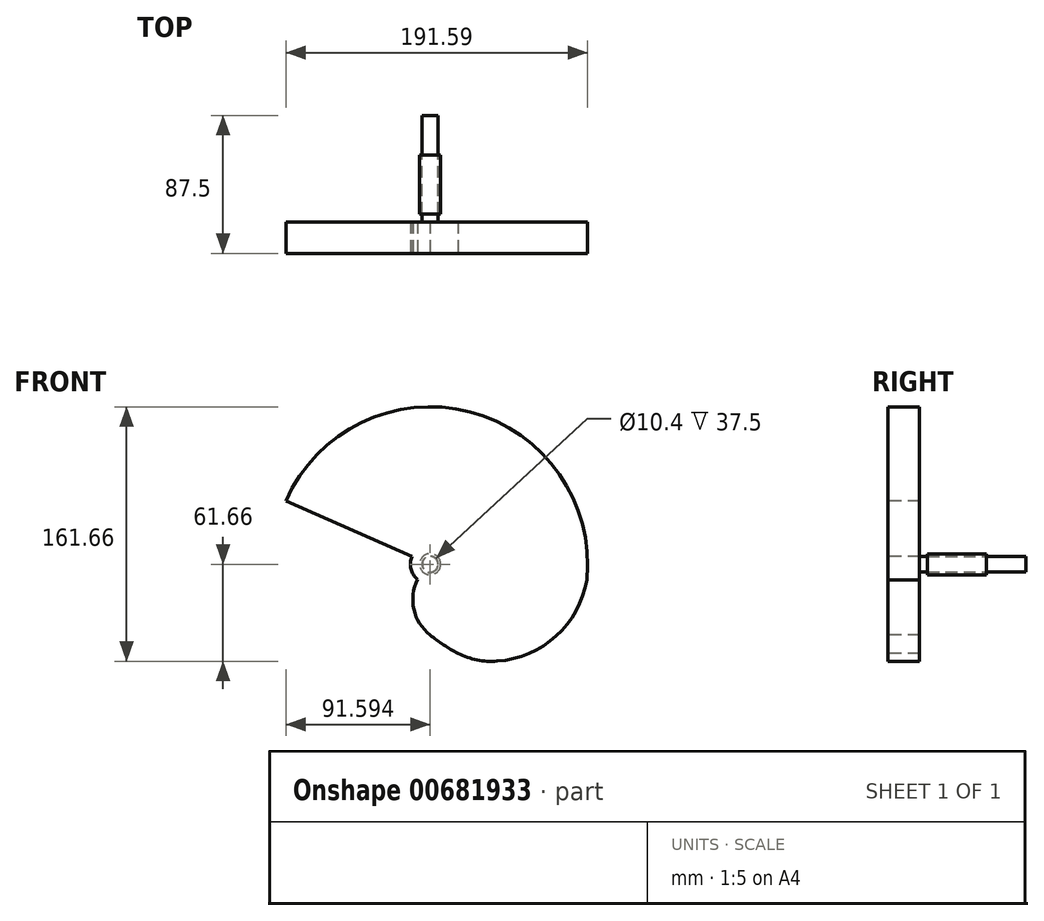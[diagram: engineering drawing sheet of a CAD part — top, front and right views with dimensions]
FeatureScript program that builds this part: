
annotation { "Feature Type Name" : "Feature", "Feature Type Description" : "" }
export const myFeature = defineFeature(function(context is Context, id is Id, definition is map)
    precondition{}
    {
        {
            var Q0;
            Q0=qCreatedBy(makeId("Front.planeOp"),FACE);
            var sketch = newSketch(context, id + "F0", { "sketchPlane" : qUnion([Q0])});
            skCircle(sketch, "E0", {"center": v(-51.72, 0) * mm, "radius": 5 * mm});
            skCircle(sketch, "E1", {"center": v(-51.72, 0) * mm, "radius": 5.2 * mm});
            skCircle(sketch, "E2", {"center": v(-51.72, 0) * mm, "radius": 6.7 * mm});
            skSolve(sketch);
        }
        {
            var Q0;
            Q0=makeQuery(id+"F0.imprint","IMPRINT",FACE,{"disambiguationData":[TD([[makeQuery(id+"F0.imprint","IMPRINT",EDGE,{"derivedFrom":sQuery(id+"F0.wireOp",EDGE,"E0")}),1.0]])]});
            var Q1;
            Q1=makeQuery(id+"F0.imprint","IMPRINT",FACE,{"disambiguationData":[TD([[makeQuery(id+"F0.imprint","IMPRINT",EDGE,{"derivedFrom":sQuery(id+"F0.wireOp",EDGE,"E1")}),-1.0]])]});
            extrude(context, id + "F1", {"entities" : qUnion([Q0, Q1]), "endBound" : BoundingType.SYMMETRIC, "depth" : 37.5 * mm, "offsetDistance" : 25 * mm});
        }
        {
            var Q0;
            Q0=makeQuery(id+"F1.opExtrude","CAP_FACE",FACE,{"disambiguationData":[OSD([sQuery(id+"F0.wireOp",EDGE,"E0")])],"isStart":false});
            extrude(context, id + "F2", {"entities" : qUnion([Q0]), "operationType" : NewBodyOperationType.ADD, "depth" : 25 * mm, "offsetDistance" : 25 * mm});
        }
        {
            var Q0;
            Q0=makeQuery(id+"F1.opExtrude","CAP_FACE",FACE,{"disambiguationData":[OSD([sQuery(id+"F0.wireOp",EDGE,"E0")])],"isStart":true});
            extrude(context, id + "F3", {"entities" : qUnion([Q0]), "operationType" : NewBodyOperationType.ADD, "depth" : 25 * mm, "offsetDistance" : 25 * mm});
        }
        {
            var Q0;
            Q0=makeQuery(id+"F2.opExtrude","CAP_FACE",FACE,{"disambiguationData":[OSD([sQuery(id+"F0.wireOp",EDGE,"E0")])],"isStart":false});
            var sketch = newSketch(context, id + "F4", { "sketchPlane" : qUnion([Q0])});
            skCircle(sketch, "E3", {"center": v(-51.72, 0) * mm, "radius": 100 * mm});
            skSolve(sketch);
        }
        {
            var Q0;
            Q0=makeQuery(id+"F4.imprint","IMPRINT",FACE,{"disambiguationData":[TD([[makeQuery(id+"F4.imprint","IMPRINT",EDGE,{"derivedFrom":sQuery(id+"F4.wireOp",EDGE,"E3")}),1.0]])]});
            extrude(context, id + "F5", {"entities" : qUnion([Q0]), "operationType" : NewBodyOperationType.ADD, "oppositeDirection" : true, "depth" : 20 * mm, "offsetDistance" : 25 * mm});
        }
        {
            var Q0;
            {var subQ0=sQuery(id+"F0.wireOp",EDGE,"E0");Q0=makeQuery(id+"F5.boolean.opBoolean","MERGE",FACE,{"derivedFrom":[makeQuery(id+"F2.opExtrude","CAP_FACE",FACE,{"disambiguationData":[OSD([subQ0])],"isStart":false}),makeQuery(id+"F5.opExtrude","CAP_FACE",FACE,{"disambiguationData":[OSD([subQ0,sQuery(id+"F4.wireOp",EDGE,"E3")])],"isStart":true})]});}
            var sketch = newSketch(context, id + "F6", { "sketchPlane" : qUnion([Q0])});
            skLineSegment(sketch, "E4", {"start": v(-51.72, 0) * mm, "end": v(-143.3, 40.14) * mm});
            skArc(sketch, "E5", {"start": v(-51.72, 0) * mm, "mid": v(-62.72, -22.48) * mm, "end": v(-51.72, -44.96) * mm});
            skArc(sketch, "E6", {"start": v(-51.72, -44.96) * mm, "mid": v(-17.5, -63.5) * mm, "end": v(21.08, -68.56) * mm});
            skArc(sketch, "E7", {"start": v(-9.11, -61.54) * mm, "mid": v(28.3, -45.57) * mm, "end": v(47.8, -9.86) * mm});
            skArc(sketch, "E8", {"start": v(-33.95, -56.6) * mm, "mid": v(-21.86, -60.75) * mm, "end": v(-9.11, -61.54) * mm});
            skCircle(sketch, "E9", {"center": v(-51.72, 0) * mm, "radius": 12.5 * mm});
            skSolve(sketch);
        }
        {
            var Q0;
            {var subQ1=makeQuery(id+"F5.opExtrude","CAP_EDGE",EDGE,{"disambiguationData":[OSD([sQuery(id+"F4.wireOp",EDGE,"E3")])],"isStart":true});var subQ8=sQuery(id+"F6.wireOp",EDGE,"E4");var subQ9=makeQuery(id+"F6.imprint","INTERSECT",VERTEX,{"derivedFrom":[subQ1,subQ8]});Q0=makeQuery(id+"F6.imprint","IMPRINT",FACE,{"disambiguationData":[TD([[makeQuery(id+"F6.imprint","IMPRINT",EDGE,{"disambiguationData":[TD([[subQ9,1.0]])],"derivedFrom":subQ8}),1.0]])]});}
            var Q1;
            {var subQ4=sQuery(id+"F6.wireOp",EDGE,"E7");Q1=makeQuery(id+"F6.imprint","IMPRINT",FACE,{"disambiguationData":[TD([[makeQuery(id+"F6.imprint","IMPRINT",EDGE,{"derivedFrom":subQ4}),-1.0]])]});}
            extrude(context, id + "F7", {"entities" : qUnion([Q0, Q1]), "operationType" : NewBodyOperationType.REMOVE, "oppositeDirection" : true, "depth" : 20 * mm, "offsetDistance" : 25 * mm});
        }
    });
